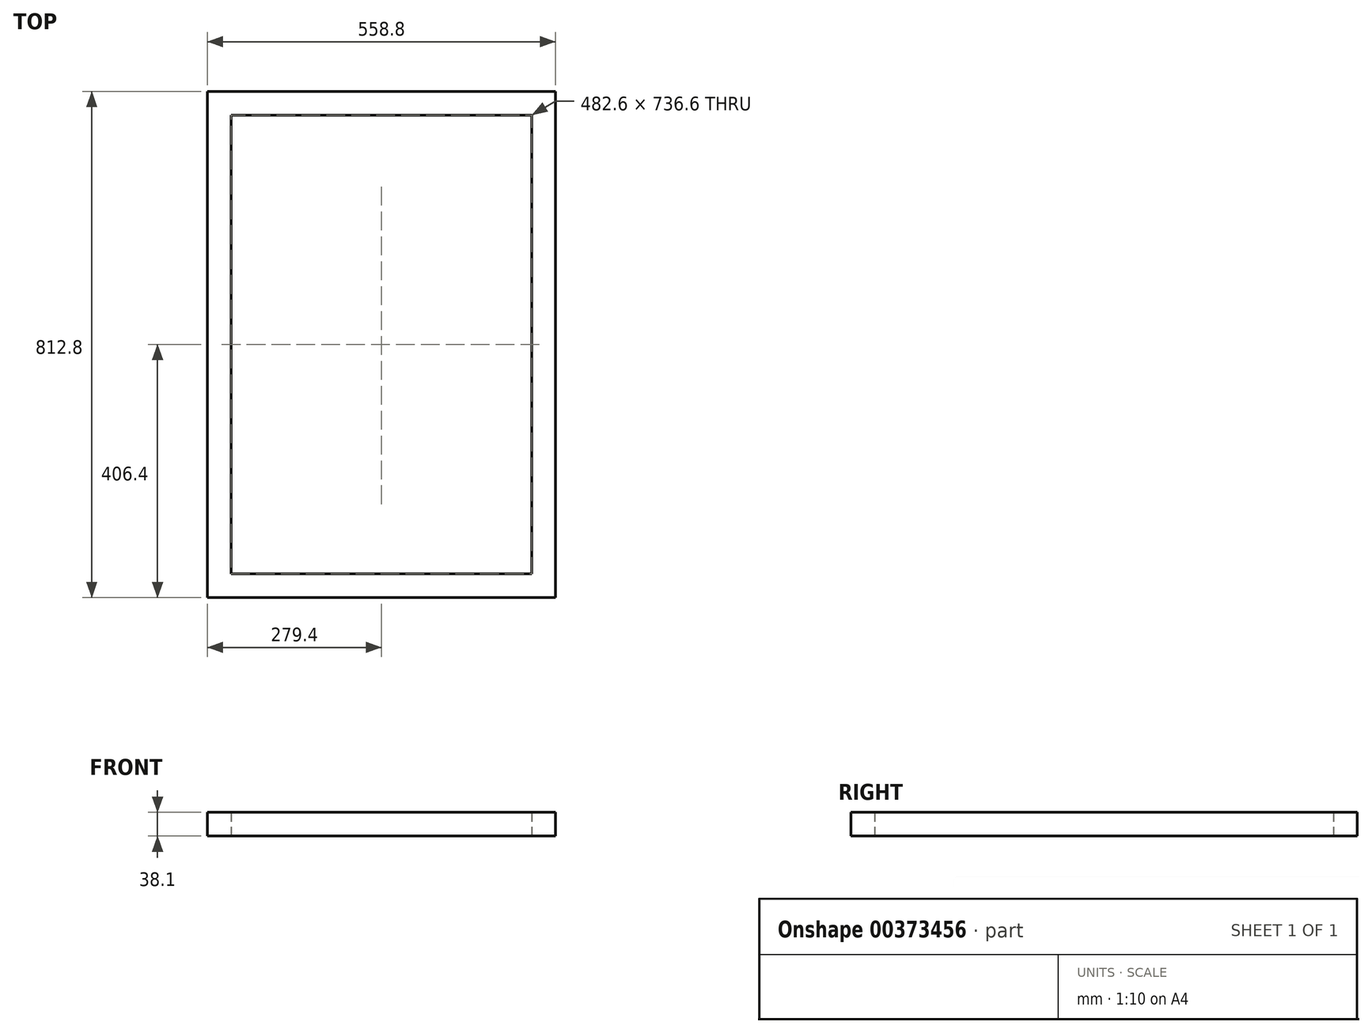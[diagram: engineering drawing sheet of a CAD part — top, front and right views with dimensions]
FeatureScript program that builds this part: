
annotation { "Feature Type Name" : "Feature", "Feature Type Description" : "" }
export const myFeature = defineFeature(function(context is Context, id is Id, definition is map)
    precondition{}
    {
        {
            var Q0;
            Q0=qCreatedBy(makeId("Top.planeOp"),FACE);
            var sketch = newSketch(context, id + "F0", { "sketchPlane" : qUnion([Q0])});
            skLineSegment(sketch, "E0.bottom", {"start": v(279.4, -406.4) * mm, "end": v(-279.4, -406.4) * mm});
            skLineSegment(sketch, "E0.top", {"start": v(279.4, 406.4) * mm, "end": v(-279.4, 406.4) * mm});
            skLineSegment(sketch, "E0.left", {"start": v(279.4, -406.4) * mm, "end": v(279.4, 406.4) * mm});
            skLineSegment(sketch, "E0.right", {"start": v(-279.4, -406.4) * mm, "end": v(-279.4, 406.4) * mm});
            skPoint(sketch, "E0.middle", {"position": v(0, 0) * mm});
            skLineSegment(sketch, "E1.bottom", {"start": v(241.3, -368.3) * mm, "end": v(-241.3, -368.3) * mm});
            skLineSegment(sketch, "E1.top", {"start": v(241.3, 368.3) * mm, "end": v(-241.3, 368.3) * mm});
            skLineSegment(sketch, "E1.left", {"start": v(241.3, -368.3) * mm, "end": v(241.3, 368.3) * mm});
            skLineSegment(sketch, "E1.right", {"start": v(-241.3, -368.3) * mm, "end": v(-241.3, 368.3) * mm});
            skSolve(sketch);
        }
        {
            var Q0;
            Q0 = qSketchRegion(id + "F0", true);
            extrude(context, id + "F1", {"entities" : qUnion([Q0]), "endBound" : BoundingType.SYMMETRIC, "depth" : 38.1 * mm});
        }
    });
